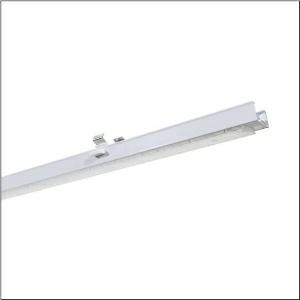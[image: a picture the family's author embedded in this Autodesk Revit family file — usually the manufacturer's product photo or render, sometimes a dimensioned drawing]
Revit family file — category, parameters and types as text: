
# Revit family: sanierungs-leuchteneinsatz_31_gen_2_51re12mb48b_1de7
name_source: partatom
category: Lighting Fixtures
units: mm (PartAtom-declared; Revit-internal decimal feet)

## family parameters
Cut with Voids When Loaded = No
Host = Face
Light Source = No
Part Type = Normal
Room Calculation Point = No
Round Connector Dimension = Use Diameter
Shared = No

## types (1)
- --- (1 x LED, 8000 lm, 50 W, 4000K)
    Apparent Load = 50 VA
    CIE Flux Codes = 65 91 98 99 100
    Color Rendering = 80
    Color Temperature = 4000K
    Default Elevation = 1800 mm
    Description = Refurbishment luminaire insert Gen.2, luminaire insert, of extruded aluminium section, coated, traffic white (RAL 9016), length: 1.472mm, width: 91mm, height: 53mm, LED rated luminous flux: 8.000lm, light colour: 840, control gear: ON/OFF Multilumen, control gear: ECG Multilumen, with system connector: socket, mains connection: 220..240V, AC/DC, 0/50..60Hz, luminous flux adjustable on luminaire in four steps (4280/5650/6950/8270lm), connected load according to luminous flux setting (24/32/40/49W), primary light control with lens, of plastic, primary optical cover: cover, of PMMA, light emission: direct distribution, protection rating (complete): IP20, insulation class (complete): insulation class I (protective earthing), certification: CE, UKCA, permissible ambient temperature for indoor applications: -20..+40°C, packaging unit: 1 piece
    Height = 58 mm
    Lamp = 1 x LED
    Lamp Light Flux = 8000 lm
    Lamp Power = 50 W
    Lamp count = 1
    Length = 1472 mm
    Luminous efficacy = 160 lm/W
    Manufacturer = Siteco
    ModVariant = No
    Model = 51RE12MB48B
    Mounting Place = Ceiling
    Mounting Type = Pendant
    Number of Poles = 1
    OnlyDefault = Yes
    Power Factor = 1
    Product Name = Sanierungs-Leuchteneinsatz 31 Gen.2
    Product group = luminaire insert
    ProductGroupID = 902
    Protection Class = Protection class I
    Protection Degree = IP 20
    RLX_Detail_Level = 1
    RlxData = <blob elided: 20313 chars, md5=e50f77b1>
    Socket = socket
    Standby Power = 0 W
    System Light Flux = 8000 lm
    System Power = 50 W
    Type Comments = factory setting: luminous flux: 100 % | (ON | ON) | 300 mA
    Type Image = l_1266702.jpg
    URL = http://relux.com
    VarID = @adj_090933
    Voltage = 0 V
    Weight = 0.00 kg
    Width = 65 mm

## geometry (parser evidence)
native form markers: Blend x4, Sweep x11
no freeform markers — native parametric forms only
